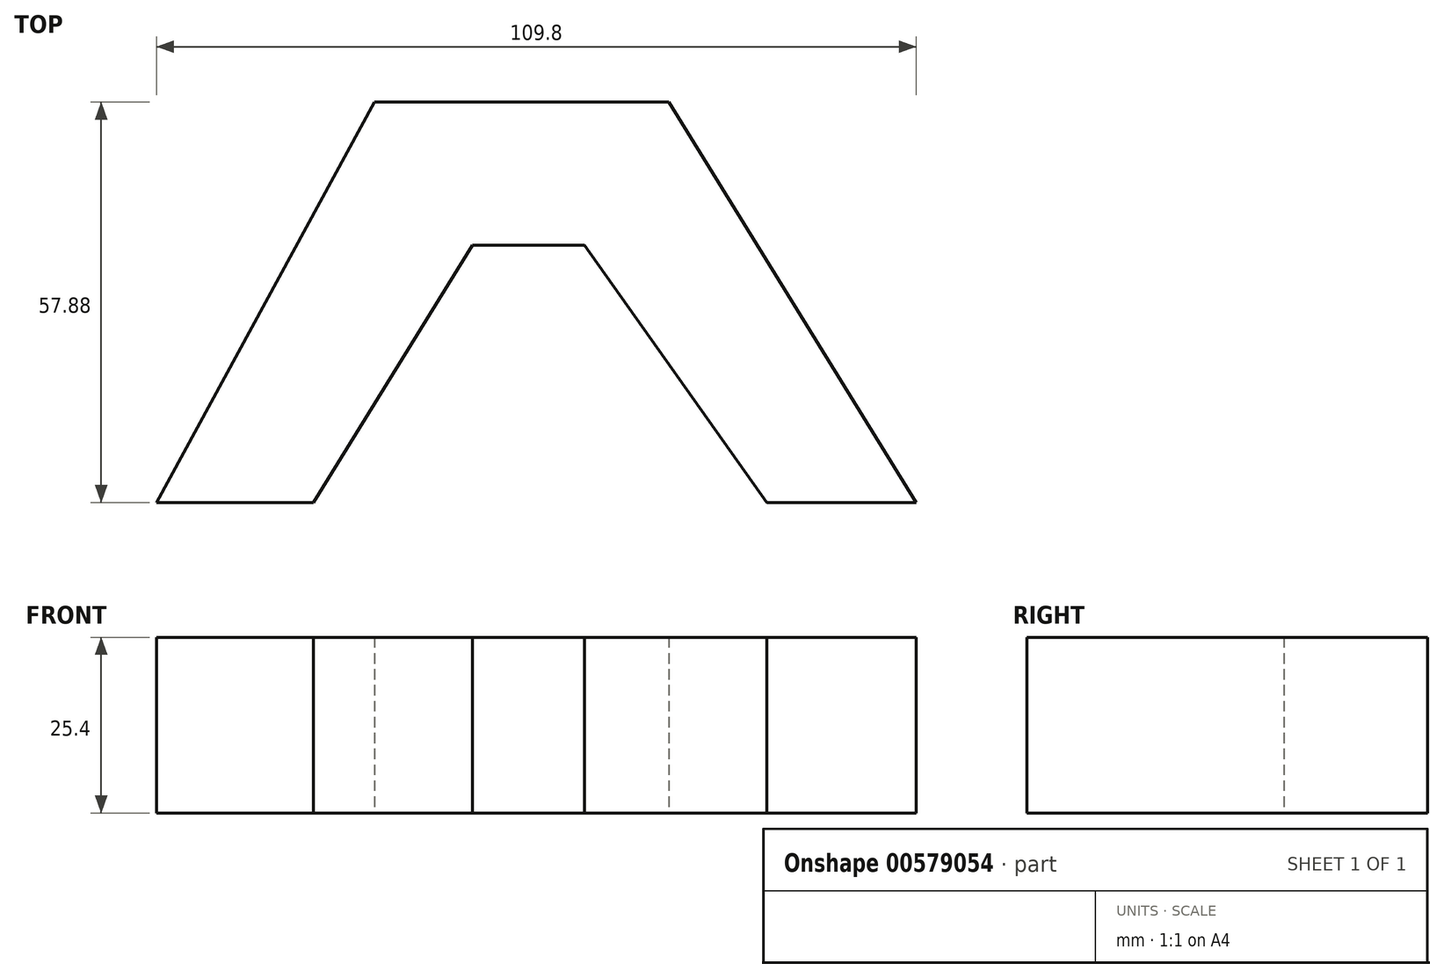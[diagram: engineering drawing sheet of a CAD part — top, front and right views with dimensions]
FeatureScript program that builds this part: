
annotation { "Feature Type Name" : "Feature", "Feature Type Description" : "" }
export const myFeature = defineFeature(function(context is Context, id is Id, definition is map)
    precondition{}
    {
        {
            var Q0;
            Q0=qCreatedBy(makeId("Top.planeOp"),FACE);
            var sketch = newSketch(context, id + "F0", { "sketchPlane" : qUnion([Q0])});
            skLineSegment(sketch, "E0", {"start": v(16.74, 31.5) * mm, "end": v(-25.82, 31.5) * mm});
            skLineSegment(sketch, "E1", {"start": v(-25.82, 31.5) * mm, "end": v(-57.31, -26.39) * mm});
            skLineSegment(sketch, "E2", {"start": v(-57.31, -26.39) * mm, "end": v(-34.61, -26.39) * mm});
            skLineSegment(sketch, "E3", {"start": v(-34.61, -26.39) * mm, "end": v(-11.63, 10.78) * mm});
            skLineSegment(sketch, "E4", {"start": v(-11.63, 10.78) * mm, "end": v(4.54, 10.78) * mm});
            skLineSegment(sketch, "E5", {"start": v(4.54, 10.78) * mm, "end": v(30.93, -26.39) * mm});
            skLineSegment(sketch, "E6", {"start": v(30.93, -26.39) * mm, "end": v(52.77, -26.39) * mm});
            skLineSegment(sketch, "E7", {"start": v(52.49, -26.39) * mm, "end": v(16.74, 31.5) * mm});
            skSolve(sketch);
        }
        {
            var Q0;
            Q0 = qSketchRegion(id + "F0", true);
            extrude(context, id + "F1", {"entities" : qUnion([Q0]), "depth" : 25.4 * mm, "offsetDistance" : 25.4 * mm});
        }
    });
